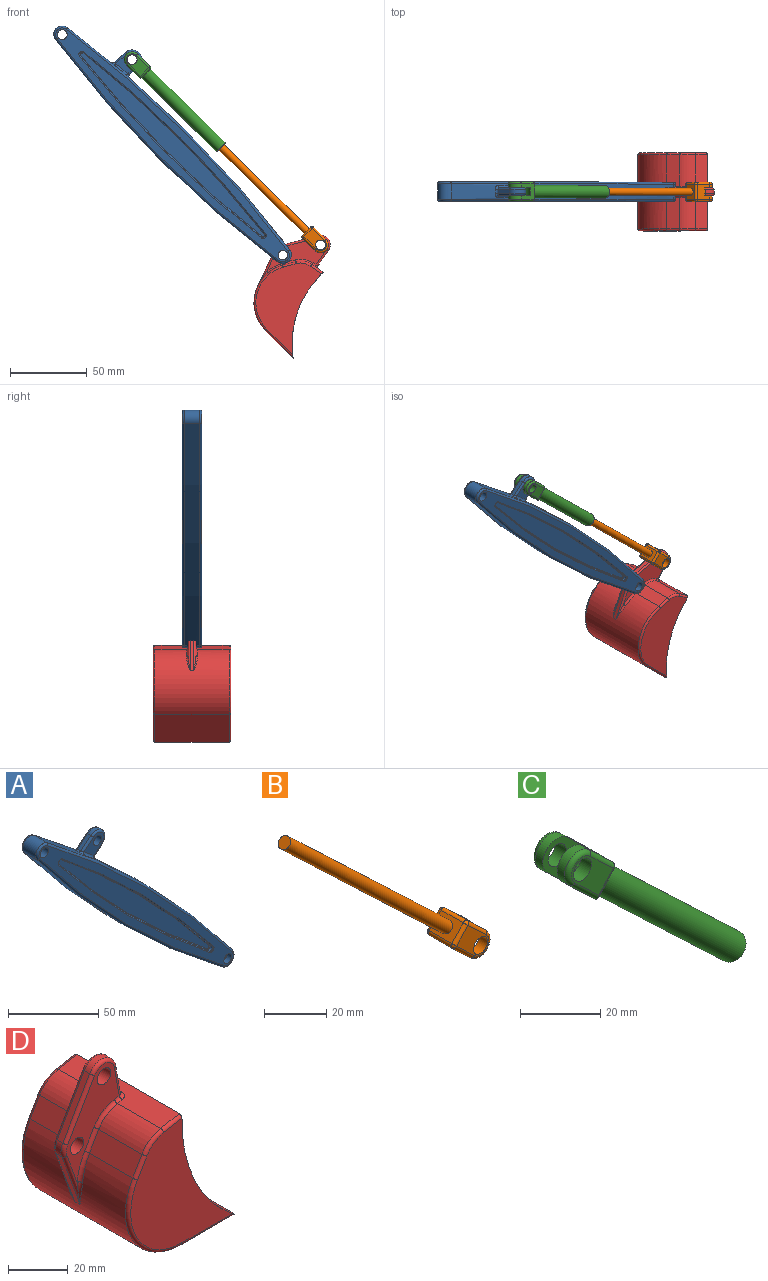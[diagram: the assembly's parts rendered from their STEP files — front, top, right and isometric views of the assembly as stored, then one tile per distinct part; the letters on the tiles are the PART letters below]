
ASSEMBLY  parts=4 mates=6
PART A: 69 faces, bbox 164.2x12.7x164.2 mm
  f0: cylinder r=5.55mm len=8.89mm, axis (0,1,0), area 40.3mm2, adj f1,f2,f16,f28
  f1: cylinder r=730.97mm len=144.78mm, axis (0,1,0), area 1917.7mm2, adj f0,f3,f4,f15,f16,f17,f27,f31
  f2: cylinder r=730.97mm len=144.78mm, axis (0,1,0), area 2071.3mm2, adj f0,f3,f4,f16,f17,f19,f30,f34
  f3: cylinder r=5.55mm len=8.89mm, axis (0,1,0), area 40.3mm2, adj f1,f2,f17,f32
  f4: cylinder r=5.55mm len=10.16mm, axis (0,1,0), area 161.3mm2, adj f1,f2,f29,f33
  f5: cylinder r=3.12mm len=12.7mm, axis (0,1,0), area 249.3mm2, adj f7,f8
  f6: cylinder r=3.17mm len=12.7mm, axis (0,1,0), area 253.4mm2, adj f7,f8
  f7: plane 152.24x152.24mm, normal (0,-1,0), area 1913mm2, adj f5,f6,f31,f32,f33,f34,f44,f45
  f8: plane 152.24x152.24mm, normal (0,1,0), area 1824.6mm2, adj f5,f6,f27,f28,f29,f30,f57,f58
  f9: plane 5.73x4.92mm, normal (0.65,0,-0.76), area 19.2mm2, adj f11,f23,f26,f64
  f10: plane 7.6x6.53mm, normal (-0.65,0,0.76), area 25.5mm2, adj f11,f21,f24,f65
  f11: cylinder r=6.35mm len=11.17mm, axis (0,1,0), area 50.7mm2, adj f9,f10,f22,f25
  f12: cylinder r=3.17mm len=6.35mm, axis (0,1,0), area 101.3mm2, adj f13,f14
  f13: plane 15.64x14.13mm, normal (0,-1,0), area 97.8mm2, adj f12,f24,f25,f26,f68
  f14: plane 15.64x14.13mm, normal (0,1,0), area 97.8mm2, adj f12,f21,f22,f23,f61
  f15: plane 7.51x5.08mm, normal (0.87,0,-0.5), area 44mm2, adj f1,f16,f17,f18
  f16: plane 16.23x11.9mm, normal (0,-1,0), area 93.2mm2, adj f0,f1,f2,f15,f18,f19,f20
  f17: plane 16.23x11.9mm, normal (0,1,0), area 93.2mm2, adj f1,f2,f3,f15,f18,f19,f20
  f18: cylinder r=6.35mm len=5.34mm, axis (0,-1,0), area 28.1mm2, adj f15,f16,f17,f19
  f19: plane 5.08x0.38mm, normal (0.94,0,0.34), area 2.1mm2, adj f2,f16,f17,f18
  f20: cylinder r=3.17mm len=6.35mm, axis (0,-1,0), area 101.3mm2, adj f16,f17
  f21: cylinder r=1.27mm len=8.43mm, axis (-0.76,0,-0.65), area 19.7mm2, adj f10,f14,f22,f63
  f22: torus R=5.08mm, axis (0,-1,0), area 36.9mm2, adj f11,f14,f21,f23
  f23: cylinder r=1.27mm len=6.87mm, axis (0.76,0,0.65), area 15.4mm2, adj f9,f14,f22,f62
  f24: cylinder r=1.27mm len=8.43mm, axis (0.76,0,0.65), area 19.7mm2, adj f10,f13,f25,f67
  f25: torus R=5.08mm, axis (0,-1,0), area 36.9mm2, adj f11,f13,f24,f26
  f26: cylinder r=1.27mm len=6.87mm, axis (-0.76,0,-0.65), area 15.4mm2, adj f9,f13,f25,f66
  f27: torus R=729.7mm, axis (0,-1,0), area 409.6mm2, adj f1,f8,f28,f29
  f28: torus R=4.28mm, axis (0,-1,0), area 29mm2, adj f0,f8,f27,f30
  f29: torus R=4.28mm, axis (0,-1,0), area 29mm2, adj f4,f8,f27,f30
  f30: torus R=729.7mm, axis (0,-1,0), area 409.6mm2, adj f2,f8,f28,f29
  f31: torus R=729.7mm, axis (0,-1,0), area 409.6mm2, adj f1,f7,f32,f33
  f32: torus R=4.28mm, axis (0,-1,0), area 29mm2, adj f3,f7,f31,f34
  f33: torus R=4.28mm, axis (0,-1,0), area 29mm2, adj f4,f7,f31,f34
  f34: torus R=729.7mm, axis (0,-1,0), area 409.6mm2, adj f2,f7,f32,f33
  f35: cylinder r=724.62mm len=118.2mm, axis (0,-1,0), area 340.4mm2, adj f38,f39,f43,f47
  f36: cylinder r=724.62mm len=118.2mm, axis (0,-1,0), area 340.4mm2, adj f38,f39,f40,f44
  f37: plane 119.98x119.98mm, normal (0,-1,0), area 1417mm2, adj f40,f41,f42,f43
  f38: cylinder r=1.52mm len=2.47mm, axis (0,1,0), area 9mm2, adj f35,f36,f42,f46
  f39: cylinder r=1.52mm len=2.47mm, axis (0,1,0), area 9mm2, adj f35,f36,f41,f45
  f40: torus R=724.11mm, axis (0,-1,0), area 133.6mm2, adj f36,f37,f41,f42
  f41: torus R=1.02mm, axis (0,-1,0), area 3.1mm2, adj f37,f39,f40,f43
  f42: torus R=1.02mm, axis (0,-1,0), area 3.1mm2, adj f37,f38,f40,f43
  f43: torus R=724.11mm, axis (0,-1,0), area 133.6mm2, adj f35,f37,f41,f42
  f44: torus R=725.13mm, axis (0,-1,0), area 133.7mm2, adj f7,f36,f45,f46
  f45: torus R=2.03mm, axis (0,-1,0), area 4mm2, adj f7,f39,f44,f47
  f46: torus R=2.03mm, axis (0,-1,0), area 4mm2, adj f7,f38,f44,f47
  f47: torus R=725.13mm, axis (0,-1,0), area 133.7mm2, adj f7,f35,f45,f46
  f48: cylinder r=724.62mm len=118.2mm, axis (0,1,0), area 255.3mm2, adj f51,f52,f56,f60
  f49: cylinder r=724.62mm len=118.2mm, axis (0,1,0), area 255.3mm2, adj f51,f52,f53,f57
  f50: plane 119.47x119.47mm, normal (0,1,0), area 1330.7mm2, adj f53,f54,f55,f56
  f51: cylinder r=1.52mm len=2.47mm, axis (0,-1,0), area 6.8mm2, adj f48,f49,f55,f59
  f52: cylinder r=1.52mm len=2.47mm, axis (0,-1,0), area 6.8mm2, adj f48,f49,f54,f58
  f53: torus R=723.86mm, axis (0,1,0), area 200.4mm2, adj f49,f50,f54,f55
  f54: torus R=0.76mm, axis (0,1,0), area 4.3mm2, adj f50,f52,f53,f56
  f55: torus R=0.76mm, axis (0,1,0), area 4.3mm2, adj f50,f51,f53,f56
  f56: torus R=723.86mm, axis (0,1,0), area 200.4mm2, adj f48,f50,f54,f55
  f57: torus R=725.38mm, axis (0,-1,0), area 200.6mm2, adj f8,f49,f58,f59
  f58: torus R=2.29mm, axis (0,-1,0), area 6.3mm2, adj f8,f52,f57,f60
  f59: torus R=2.29mm, axis (0,-1,0), area 6.3mm2, adj f8,f51,f57,f60
  f60: torus R=725.38mm, axis (0,-1,0), area 200.6mm2, adj f8,f48,f58,f59
  f61: torus R=732.5mm, axis (0,-1,0), area 24.6mm2, adj f1,f14,f62,f63
  f62: bspline ~3.41x3.16mm, area 7.2mm2, adj f1,f23,f61,f64
  f63: bspline ~3.41x3.41mm, area 6.6mm2, adj f1,f21,f61,f65
  f64: cylinder r=1.52mm len=2.54mm, axis (0,1,0), area 6.6mm2, adj f1,f9,f62,f66
  f65: cylinder r=1.52mm len=2.54mm, axis (0,1,0), area 5.4mm2, adj f1,f10,f63,f67
  f66: bspline ~3.41x3.16mm, area 7.2mm2, adj f1,f26,f64,f68
  f67: bspline ~3.41x3.41mm, area 6.6mm2, adj f1,f24,f65,f68
  f68: torus R=732.5mm, axis (0,-1,0), area 24.6mm2, adj f1,f13,f66,f67
PART B: 29 faces, bbox 90x12.7x85.9 mm
  f0: plane 10.16x8.29mm, normal (0.69,0,0.73), area 96.8mm2, adj f2,f5,f12,f13,f14,f15,f20,f25
  f1: plane 10.16x8.29mm, normal (-0.69,0,-0.73), area 89.2mm2, adj f2,f5,f11,f13,f14,f19,f24,f28
  f2: cylinder r=5.08mm len=8.76mm, axis (0,1,0), area 40.5mm2, adj f0,f1,f13,f27
  f3: cylinder r=3.17mm len=6.35mm, axis (0,1,0), area 76mm2, adj f8,f13
  f4: plane 10.16x5.52mm, normal (-0.73,0,0.69), area 59.7mm2, adj f9,f18,f20,f23,f24
  f5: cylinder r=5.08mm len=8.76mm, axis (0,1,0), area 40.5mm2, adj f0,f1,f14,f16
  f6: cylinder r=3.17mm len=6.35mm, axis (0,1,0), area 76mm2, adj f7,f14
  f7: plane 14.72x14.44mm, normal (0,-1,0), area 78.2mm2, adj f6,f15,f16,f18,f19
  f8: plane 14.72x14.44mm, normal (0,1,0), area 78.2mm2, adj f3,f23,f25,f27,f28
  f9: cylinder r=2.37mm len=76.94mm, axis (0.73,0,-0.69), area 1516.1mm2, adj f4,f10
  f10: plane 4.75x3.44mm, normal (-0.73,0,0.69), area 17.7mm2, adj f9
  f11: plane 5.08x3.2mm, normal (0.87,0,-0.5), area 18.8mm2, adj f1,f12,f13,f14
  f12: cylinder r=6.35mm len=6.24mm, axis (0,-1,0), area 37.5mm2, adj f0,f11,f13,f14
  f13: plane 12.43x11.43mm, normal (0,-1,0), area 67.2mm2, adj f0,f1,f2,f3,f11,f12
  f14: plane 12.43x11.43mm, normal (0,1,0), area 67.2mm2, adj f0,f1,f5,f6,f11,f12
  f15: cylinder r=1.27mm len=9.16mm, axis (0.73,0,-0.69), area 22.8mm2, adj f0,f7,f16,f17
  f16: torus R=3.81mm, axis (0,-1,0), area 28.9mm2, adj f5,f7,f15,f19
  f17: sphere r=1.27mm, area 2.5mm2, adj f15,f18,f20
  f18: cylinder r=1.27mm len=6.4mm, axis (0.69,0,0.73), area 15.2mm2, adj f4,f7,f17,f21
  f19: cylinder r=1.27mm len=9.16mm, axis (-0.73,0,0.69), area 22.8mm2, adj f1,f7,f16,f21
  f20: cylinder r=1.27mm len=10.16mm, axis (0,1,0), area 20.3mm2, adj f0,f4,f17,f22
  f21: sphere r=1.27mm, area 2.5mm2, adj f18,f19,f24
  f22: sphere r=1.27mm, area 2.5mm2, adj f20,f23,f25
  f23: cylinder r=1.27mm len=6.4mm, axis (-0.69,0,-0.73), area 15.2mm2, adj f4,f8,f22,f26
  f24: cylinder r=1.27mm len=10.16mm, axis (0,-1,0), area 20.3mm2, adj f1,f4,f21,f26
  f25: cylinder r=1.27mm len=9.16mm, axis (-0.73,0,0.69), area 22.8mm2, adj f0,f8,f22,f27
  f26: sphere r=1.27mm, area 2.5mm2, adj f23,f24,f28
  f27: torus R=3.81mm, axis (0,-1,0), area 28.9mm2, adj f2,f8,f25,f28
  f28: cylinder r=1.27mm len=9.16mm, axis (0.73,0,-0.69), area 22.8mm2, adj f1,f8,f26,f27
PART C: 30 faces, bbox 67.3x12.7x64.5 mm
  f0: cylinder r=5.08mm len=8.76mm, axis (0,1,0), area 40.5mm2, adj f2,f4,f23,f29
  f1: cylinder r=3.17mm len=6.35mm, axis (0,1,0), area 76mm2, adj f8,f29
  f2: plane 10.16x8.32mm, normal (0.69,0,0.73), area 75.3mm2, adj f0,f3,f16,f18,f19,f20,f21,f27
  f3: cylinder r=5.08mm len=8.76mm, axis (0,1,0), area 40.5mm2, adj f2,f4,f14,f28
  f4: plane 10.16x9.21mm, normal (-0.69,0,-0.73), area 83mm2, adj f0,f3,f6,f13,f25,f26,f28,f29
  f5: cylinder r=3.17mm len=6.35mm, axis (0,1,0), area 76mm2, adj f7,f28
  f6: plane 10.16x6.45mm, normal (0.73,0,-0.69), area 37.5mm2, adj f4,f9,f15,f18,f20,f24
  f7: plane 14.72x14.44mm, normal (0,-1,0), area 78.2mm2, adj f5,f13,f14,f15,f16
  f8: plane 14.72x14.44mm, normal (0,1,0), area 78.2mm2, adj f1,f21,f23,f24,f25
  f9: cylinder r=4.13mm len=55.41mm, axis (-0.73,0,0.69), area 1778.5mm2, adj f6,f10,f19
  f10: plane 8.26x5.99mm, normal (0.73,0,-0.69), area 35.8mm2, adj f9,f11
  f11: cylinder r=2.37mm len=46.92mm, axis (0.73,0,-0.69), area 898.3mm2, adj f10,f12
  f12: plane 4.75x3.44mm, normal (0.73,0,-0.69), area 17.7mm2, adj f11
  f13: cylinder r=1.27mm len=10.08mm, axis (-0.73,0,0.69), area 24.4mm2, adj f4,f7,f14,f15
  f14: torus R=3.81mm, axis (0,-1,0), area 28.9mm2, adj f3,f7,f13,f16
  f15: cylinder r=1.27mm len=7.32mm, axis (-0.69,0,-0.73), area 16.8mm2, adj f6,f7,f13,f17
  f16: cylinder r=1.27mm len=9.16mm, axis (0.73,0,-0.69), area 22.8mm2, adj f2,f7,f14,f17
  f17: sphere r=1.27mm, area 2.5mm2, adj f15,f16,f18
  f18: cylinder r=1.27mm len=3.49mm, axis (0,-1,0), area 7mm2, adj f2,f6,f17,f19
  f19: bspline ~3.83x1.92mm, area 5.7mm2, adj f2,f9,f18,f20
  f20: cylinder r=1.27mm len=3.49mm, axis (0,-1,0), area 7mm2, adj f2,f6,f19,f22
  f21: cylinder r=1.27mm len=9.16mm, axis (-0.73,0,0.69), area 22.8mm2, adj f2,f8,f22,f23
  f22: sphere r=1.27mm, area 2.5mm2, adj f20,f21,f24
  f23: torus R=3.81mm, axis (0,-1,0), area 28.9mm2, adj f0,f8,f21,f25
  f24: cylinder r=1.27mm len=7.32mm, axis (0.69,0,0.73), area 16.8mm2, adj f6,f8,f22,f25
  f25: cylinder r=1.27mm len=10.08mm, axis (0.73,0,-0.69), area 24.4mm2, adj f4,f8,f23,f24
  f26: plane 5.08x3.14mm, normal (-0.65,0,0.76), area 21mm2, adj f4,f27,f28,f29
  f27: cylinder r=9.53mm len=5.36mm, axis (0,1,0), area 32.1mm2, adj f2,f26,f28,f29
  f28: plane 15x14.42mm, normal (0,1,0), area 102.2mm2, adj f2,f3,f4,f5,f26,f27
  f29: plane 15x14.42mm, normal (0,-1,0), area 102.2mm2, adj f0,f1,f2,f4,f26,f27
PART D: 59 faces, bbox 58.9x50.8x73.8 mm
  f0: cylinder r=25.4mm len=48.26mm, axis (0,1,0), area 2420.6mm2, adj f2,f5,f6,f21,f27,f29,f47,f48
  f1: plane 48.26x8.89mm, normal (-0.17,0,0.98), area 401mm2, adj f3,f4,f9,f35,f36,f38,f40,f42
  f2: plane 20.32x7.57mm, normal (-0.87,0,0.5), area 177.6mm2, adj f0,f3,f31,f56
  f3: cylinder r=12.7mm len=20.32mm, axis (0,1,0), area 225.2mm2, adj f1,f2,f33,f55
  f4: cylinder r=63.5mm len=53.4mm, axis (0,1,0), area 614.6mm2, adj f1,f5,f7,f8,f11,f12,f14,f15
  f5: plane 48.26x25.4mm, normal (0,0,-1), area 1225.8mm2, adj f0,f4,f49,f58
  f6: plane 20.32x7.57mm, normal (-0.87,0,0.5), area 177.6mm2, adj f0,f9,f46,f51
  f7: plane 50.83x47.89mm, normal (0,-1,0), area 1317.9mm2, adj f4,f49,f50,f51,f52,f53
  f8: plane 50.83x47.89mm, normal (0,1,0), area 1317.9mm2, adj f4,f54,f55,f56,f57,f58
  f9: cylinder r=12.7mm len=20.32mm, axis (0,1,0), area 225.2mm2, adj f1,f6,f44,f52
  f10: cylinder r=22.86mm len=45.72mm, axis (0,1,0), area 2189mm2, adj f11,f13,f14,f15
  f11: plane 45.72x22.23mm, normal (0,0,1), area 1016.4mm2, adj f4,f10,f14,f15
  f12: plane 45.72x8.39mm, normal (0.17,0,-0.98), area 389.6mm2, adj f4,f14,f15,f16
  f13: plane 45.72x7.57mm, normal (0.87,0,-0.5), area 399.7mm2, adj f10,f14,f15,f16
  f14: plane 48.27x45.09mm, normal (0,1,0), area 1192.2mm2, adj f4,f10,f11,f12,f13,f16
  f15: plane 48.27x45.09mm, normal (0,-1,0), area 1192.2mm2, adj f4,f10,f11,f12,f13,f16
  f16: cylinder r=10.16mm len=45.72mm, axis (0,1,0), area 405.4mm2, adj f12,f13,f14,f15
  f17: plane 12.22x2.54mm, normal (0.98,0,0.17), area 31.5mm2, adj f18,f34,f37,f38
  f18: cylinder r=6.35mm len=11.75mm, axis (0,-1,0), area 39.4mm2, adj f17,f19,f32,f39
  f19: plane 22x12.7mm, normal (-0.87,0,0.5), area 64.5mm2, adj f18,f20,f30,f41
  f20: cylinder r=6.35mm len=5.34mm, axis (0,-1,0), area 14.1mm2, adj f19,f21,f28,f43
  f21: plane 23.93x8.7mm, normal (-0.94,0,-0.34), area 64.7mm2, adj f0,f20,f26,f45
  f22: cylinder r=3.17mm len=6.35mm, axis (0,-1,0), area 101.3mm2, adj f24,f25
  f23: cylinder r=3.17mm len=6.35mm, axis (0,-1,0), area 101.3mm2, adj f24,f25
  f24: plane 42.07x24.94mm, normal (0,1,0), area 361.3mm2, adj f22,f23,f26,f28,f29,f30,f31,f32
  f25: plane 42.07x24.94mm, normal (0,-1,0), area 361.3mm2, adj f22,f23,f37,f39,f41,f42,f43,f44
  f26: cylinder r=1.27mm len=24.37mm, axis (-0.34,0,0.94), area 38.7mm2, adj f21,f24,f27,f28
  f27: bspline ~12.67x2.84mm, area 10.9mm2, adj f0,f26,f29
  f28: torus R=5.08mm, axis (0,-1,0), area 10.2mm2, adj f20,f24,f26,f30
  f29: torus R=26.67mm, axis (0,-1,0), area 22.3mm2, adj f0,f24,f27,f31
  f30: cylinder r=1.27mm len=22.63mm, axis (0.5,0,0.87), area 50.7mm2, adj f19,f24,f28,f32
  f31: cylinder r=1.27mm len=8.21mm, axis (-0.5,0,-0.87), area 17.4mm2, adj f2,f24,f29,f33
  f32: torus R=5.08mm, axis (0,-1,0), area 28.7mm2, adj f18,f24,f30,f34
  f33: torus R=13.97mm, axis (0,-1,0), area 22.9mm2, adj f3,f24,f31,f35
  f34: cylinder r=1.27mm len=12.44mm, axis (0.17,0,-0.98), area 24.7mm2, adj f17,f24,f32,f36
  f35: cylinder r=1.27mm len=2.53mm, axis (-0.98,0,-0.17), area 4.7mm2, adj f1,f24,f33,f36
  f36: torus R=2.54mm, axis (-0.17,0,0.98), area 5.4mm2, adj f1,f34,f35,f38
  f37: cylinder r=1.27mm len=12.44mm, axis (-0.17,0,0.98), area 24.7mm2, adj f17,f25,f39,f40
  f38: cylinder r=1.27mm len=2.54mm, axis (0,-1,0), area 5.1mm2, adj f1,f17,f36,f40
  f39: torus R=5.08mm, axis (0,-1,0), area 28.7mm2, adj f18,f25,f37,f41
  f40: torus R=2.54mm, axis (-0.17,0,0.98), area 5.4mm2, adj f1,f37,f38,f42
  f41: cylinder r=1.27mm len=22.63mm, axis (-0.5,0,-0.87), area 50.7mm2, adj f19,f25,f39,f43
  f42: cylinder r=1.27mm len=2.53mm, axis (0.98,0,0.17), area 4.7mm2, adj f1,f25,f40,f44
  f43: torus R=5.08mm, axis (0,-1,0), area 10.2mm2, adj f20,f25,f41,f45
  f44: torus R=13.97mm, axis (0,-1,0), area 22.9mm2, adj f9,f25,f42,f46
  f45: cylinder r=1.27mm len=24.37mm, axis (0.34,0,-0.94), area 38.7mm2, adj f21,f25,f43,f47
  f46: cylinder r=1.27mm len=8.21mm, axis (0.5,0,0.87), area 17.4mm2, adj f6,f25,f44,f48
  f47: bspline ~12.67x2.84mm, area 10.9mm2, adj f0,f45,f48
  f48: torus R=26.67mm, axis (0,-1,0), area 22.3mm2, adj f0,f25,f46,f47
  f49: cylinder r=1.27mm len=25.4mm, axis (-1,0,0), area 49.5mm2, adj f4,f5,f7,f50
  f50: torus R=24.13mm, axis (0,-1,0), area 104.2mm2, adj f0,f7,f49,f51
  f51: cylinder r=1.27mm len=8.21mm, axis (0.5,0,0.87), area 17.4mm2, adj f6,f7,f50,f52
  f52: torus R=11.43mm, axis (0,-1,0), area 21.3mm2, adj f7,f9,f51,f53
  f53: cylinder r=1.27mm len=9.11mm, axis (0.98,0,0.17), area 17.7mm2, adj f1,f4,f7,f52
  f54: cylinder r=1.27mm len=9.11mm, axis (-0.98,0,-0.17), area 17.7mm2, adj f1,f4,f8,f55
  f55: torus R=11.43mm, axis (0,-1,0), area 21.3mm2, adj f3,f8,f54,f56
  f56: cylinder r=1.27mm len=8.21mm, axis (-0.5,0,-0.87), area 17.4mm2, adj f2,f8,f55,f57
  f57: torus R=24.13mm, axis (0,-1,0), area 104.2mm2, adj f0,f8,f56,f58
  f58: cylinder r=1.27mm len=25.4mm, axis (1,0,0), area 49.5mm2, adj f4,f5,f8,f57
PLACE A t=(-26.82,14.85,14.83)mm fixed
PLACE B rot(axis=(0,1,0),1deg) t=(-15.69,14.85,-0.78)mm
PLACE C rot(axis=(0,1,0),1deg) t=(-29.37,14.85,12.67)mm
PLACE D rot(axis=(0,1,0),44.9deg) t=(-46.87,14.85,1.13)mm
MATE cylindrical B.f2 <-> D.f18  axis (0,1,0) through (-28.9,21.2,38.87)mm
MATE cylindrical D.f20 <-> A.f0  axis (0,-1,0) through (-53.42,12.31,32.25)mm
MATE slider B.f9 <-> C.f9  axis (0.71,0,-0.7) through (-74.17,14.85,83.4)mm
MATE planar A.f16 <-> D.f24  axis (0,-1,0) through (-59.39,17.39,30.08)mm
MATE planar C.f29 <-> A.f14  axis (0,-1,0) through (-149.24,17.39,157.18)mm
MATE cylindrical C.f0 <-> A.f11  axis (0,-1,0) through (-151.59,8.5,159.56)mm
